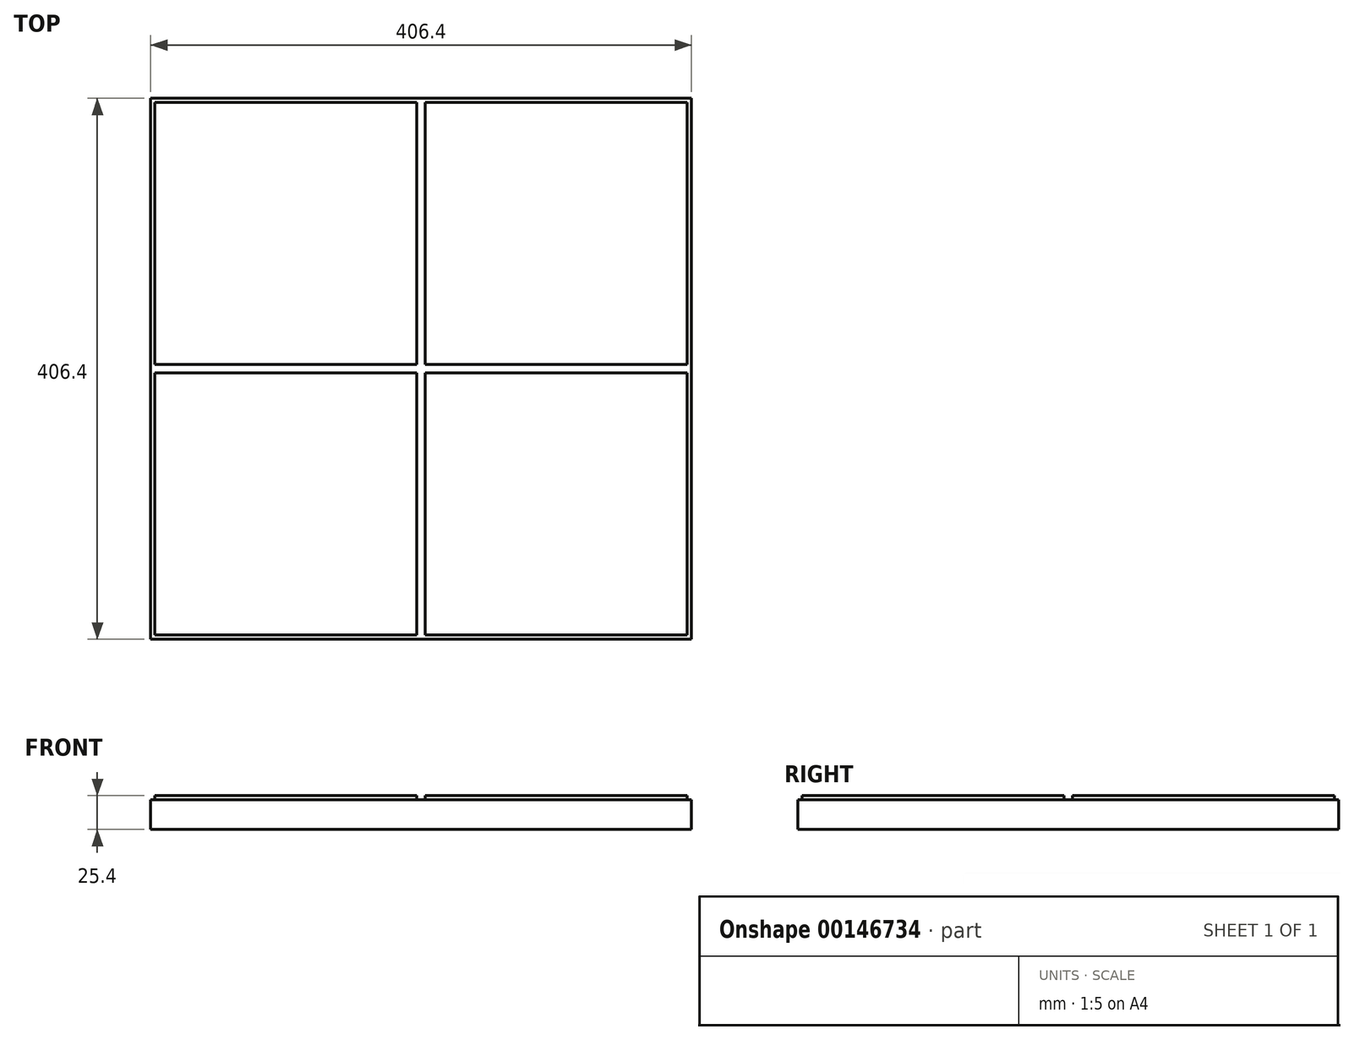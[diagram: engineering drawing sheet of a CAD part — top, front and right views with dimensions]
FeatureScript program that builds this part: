
annotation { "Feature Type Name" : "Feature", "Feature Type Description" : "" }
export const myFeature = defineFeature(function(context is Context, id is Id, definition is map)
    precondition{}
    {
        {
            var Q0;
            Q0=qCreatedBy(makeId("Top.planeOp"),FACE);
            var sketch = newSketch(context, id + "F0", { "sketchPlane" : qUnion([Q0])});
            skLineSegment(sketch, "E0.bottom", {"start": v(-203.2, -203.2) * mm, "end": v(203.2, -203.2) * mm});
            skLineSegment(sketch, "E0.top", {"start": v(-203.2, 203.2) * mm, "end": v(203.2, 203.2) * mm});
            skLineSegment(sketch, "E0.left", {"start": v(-203.2, -203.2) * mm, "end": v(-203.2, 203.2) * mm});
            skLineSegment(sketch, "E0.right", {"start": v(203.2, -203.2) * mm, "end": v(203.2, 203.2) * mm});
            skPoint(sketch, "E0.middle", {"position": v(0, 0) * mm});
            skSolve(sketch);
        }
        {
            var Q0;
            Q0 = qSketchRegion(id + "F0", true);
            var Q1;
            Q1 = qSketchRegion(id + "F2", true);
            extrude(context, id + "F1", {"entities" : qUnion([Q0, Q1]), "oppositeDirection" : true, "depth" : 25.4 * mm});
        }
        {
            var Q0;
            Q0=qCreatedBy(makeId("Top.planeOp"),FACE);
            var sketch = newSketch(context, id + "F2", { "sketchPlane" : qUnion([Q0])});
            skPoint(sketch, "E1.middle", {"position": v(0, 0) * mm});
            skLineSegment(sketch, "E2.bottom", {"start": v(200.03, -200.02) * mm, "end": v(3.17, -200.03) * mm});
            skLineSegment(sketch, "E2.top", {"start": v(200.02, 200.03) * mm, "end": v(3.18, 200.03) * mm});
            skLineSegment(sketch, "E2.left", {"start": v(200.03, -200.02) * mm, "end": v(200.03, -3.17) * mm});
            skLineSegment(sketch, "E2.right", {"start": v(-200.02, -200.03) * mm, "end": v(-200.03, -3.17) * mm});
            skLineSegment(sketch, "E3.bottom", {"start": v(-200.03, -3.18) * mm, "end": v(-3.18, -3.18) * mm});
            skLineSegment(sketch, "E3.top", {"start": v(-200.02, 3.17) * mm, "end": v(-3.18, 3.17) * mm});
            skLineSegment(sketch, "E4.left", {"start": v(3.18, 200.03) * mm, "end": v(3.18, 3.17) * mm});
            skLineSegment(sketch, "E4.right", {"start": v(-3.17, 200.03) * mm, "end": v(-3.18, 3.17) * mm});
            skLineSegment(sketch, "E5.trimOffspring", {"start": v(3.18, -3.18) * mm, "end": v(200.03, -3.18) * mm});
            skLineSegment(sketch, "E6.trimOffspring", {"start": v(3.18, -3.18) * mm, "end": v(3.17, -200.03) * mm});
            skLineSegment(sketch, "E7.trimOffspring", {"start": v(3.18, 3.17) * mm, "end": v(200.03, 3.17) * mm});
            skLineSegment(sketch, "E8.trimOffspring", {"start": v(-3.18, -3.18) * mm, "end": v(-3.18, -200.03) * mm});
            skLineSegment(sketch, "E9.trimOffspring", {"start": v(-200.02, 3.17) * mm, "end": v(-200.03, 200.02) * mm});
            skPoint(sketch, "E3.left.end.orphan", {"position": v(-238.11, 3.17) * mm});
            skPoint(sketch, "E3.left.start.orphan", {"position": v(-238.11, -3.18) * mm});
            skLineSegment(sketch, "E10.trimOffspring", {"start": v(-3.17, 200.03) * mm, "end": v(-200.03, 200.03) * mm});
            skPoint(sketch, "E4.bottom.end.orphan", {"position": v(-3.17, 226.8) * mm});
            skPoint(sketch, "E4.bottom.start.orphan", {"position": v(3.18, 226.8) * mm});
            skLineSegment(sketch, "E11.trimOffspring", {"start": v(-3.18, -200.03) * mm, "end": v(-200.02, -200.03) * mm});
            skPoint(sketch, "E4.top.end.orphan", {"position": v(-3.18, -226.8) * mm});
            skPoint(sketch, "E4.top.start.orphan", {"position": v(3.17, -226.8) * mm});
            skPoint(sketch, "E3.right.end.orphan", {"position": v(238.11, 3.17) * mm});
            skPoint(sketch, "E3.right.start.orphan", {"position": v(238.11, -3.18) * mm});
            skLineSegment(sketch, "E12.trimOffspring", {"start": v(200.03, 3.17) * mm, "end": v(200.03, 200.03) * mm});
            skLineSegment(sketch, "E13.bottom", {"start": v(212.68, -214.28) * mm, "end": v(-212.68, -214.28) * mm});
            skLineSegment(sketch, "E13.top", {"start": v(212.68, 214.28) * mm, "end": v(-212.68, 214.28) * mm});
            skLineSegment(sketch, "E13.left", {"start": v(212.68, -214.28) * mm, "end": v(212.68, 214.28) * mm});
            skLineSegment(sketch, "E13.right", {"start": v(-212.68, -214.28) * mm, "end": v(-212.68, 214.28) * mm});
            skSolve(sketch);
        }
        {
            var Q0;
            Q0 = qSketchRegion(id + "F2", true);
            extrude(context, id + "F3", {"entities" : qUnion([Q0]), "operationType" : NewBodyOperationType.REMOVE, "oppositeDirection" : true, "depth" : 3.05 * mm});
        }
    });
